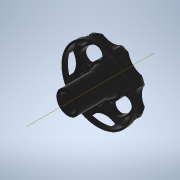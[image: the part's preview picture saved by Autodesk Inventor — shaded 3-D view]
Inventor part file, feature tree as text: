
AUTODESK INVENTOR PART (.ipt)
format: ipt  version: 2022 (Build 260153000, 153)  size: 308,736 bytes
history: native  units: in
note: dims shown in document units (in); Inventor stores cm internally (conversion verified against a paired STEP export)
features: sketch x2, revolve x1, extrude x1, plane x1
ambient origin geometry x8: Origin, YZ Plane, XZ Plane, XY Plane, X Axis, Y Axis, Z Axis, Center Point
bodies: Solid1 (feature_tree)
feature tree (5):
  revolve  "Revolution1"  [1 undecoded]
  extrude  "Extrusion1"  Depth=0.0787in
  plane  "Work Plane1"
  sketch  "Sketch1"  dims[d0=0.8366in d1=0.2559in]
  sketch  "Sketch2"  dims[d2=0.7874in d3=0.0787in d4=0.063in d5=0.0394in d6=0.0394in d7=0.0315in d8=0.0197in d9=0.0492in d10=0.1476in d11=0.315in d12=0.2756in d13=0.1969in d14=0.1575in d15=0.1575in d16=0.7087in d17=0.1969in d18=0.1575in d19=0.2657in d20=90.0deg d21=0.9843in d22=0.1181in d23=0.2756in d24=0.1718in d25=0.0197in d26=0.2749in d27=0.7874in d28=1.378in d29=1.5748in d31=360.0deg d33=3.1496in d35=360.0deg d37=0.2362in d38=0.0in]
note: 1 required parameter value undecoded (feature->parameter linkage not recoverable at this tier; creation-order binding heuristic only, values carry confidence <= 0.55)
